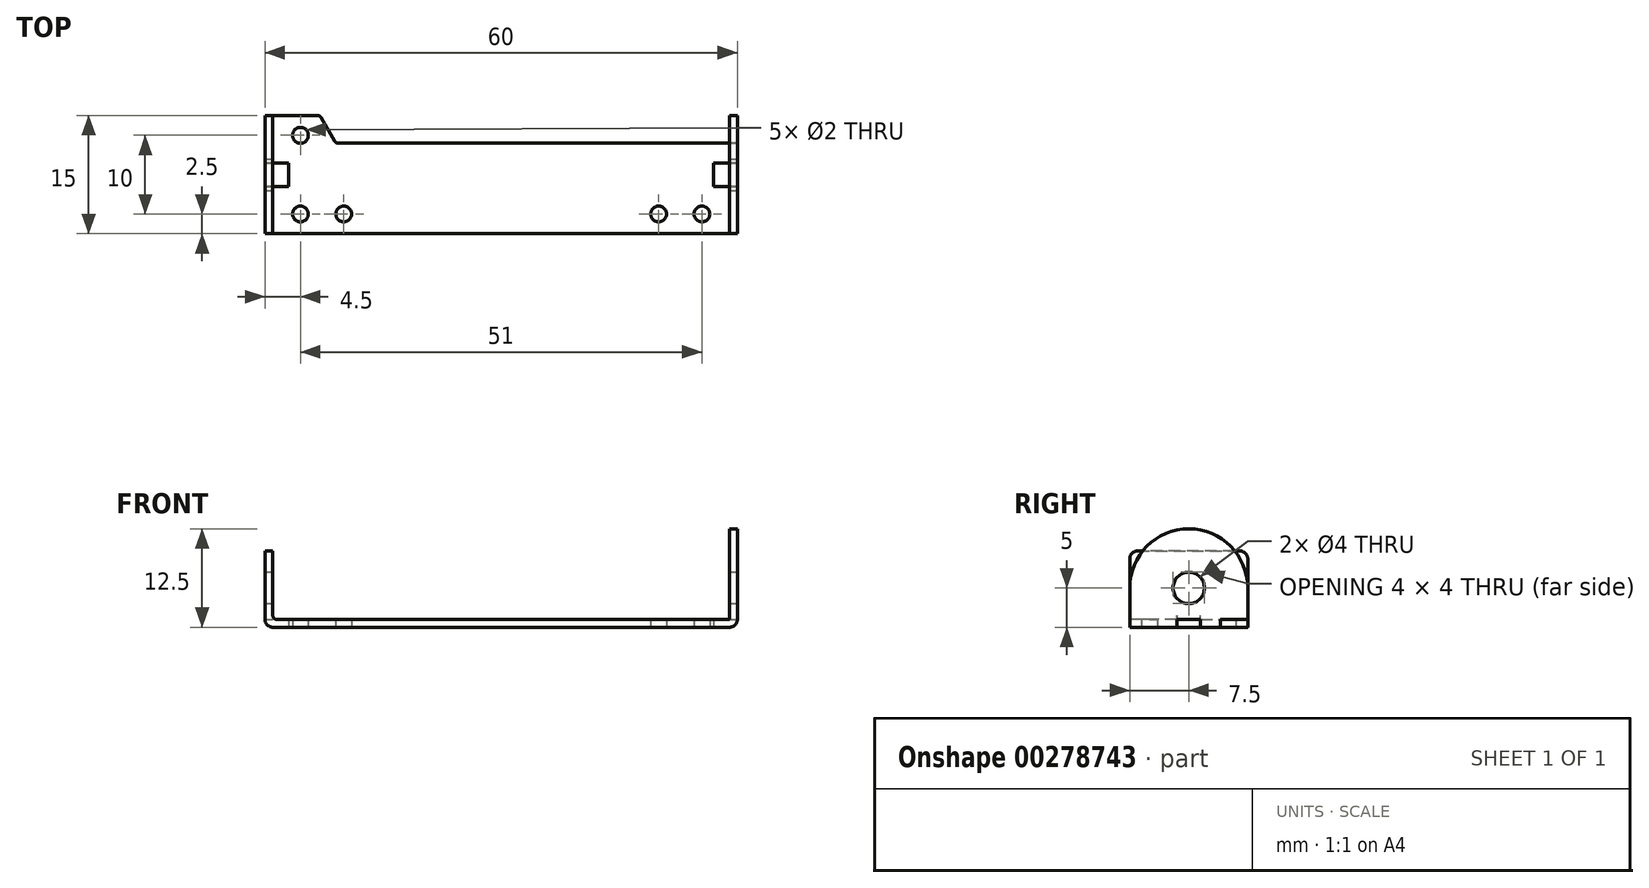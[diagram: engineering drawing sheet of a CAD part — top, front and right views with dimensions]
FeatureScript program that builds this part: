
annotation { "Feature Type Name" : "Feature", "Feature Type Description" : "" }
export const myFeature = defineFeature(function(context is Context, id is Id, definition is map)
    precondition{}
    {
        {
            var Q0;
            Q0=qCreatedBy(makeId("Top.planeOp"),FACE);
            var sketch = newSketch(context, id + "F0", { "sketchPlane" : qUnion([Q0])});
            skLineSegment(sketch, "E0.bottom", {"start": v(0, 0) * mm, "end": v(60, 0) * mm});
            skLineSegment(sketch, "E0.top", {"start": v(0, 15) * mm, "end": v(60, 15) * mm});
            skLineSegment(sketch, "E0.left", {"start": v(0, 0) * mm, "end": v(0, 15) * mm});
            skLineSegment(sketch, "E0.right", {"start": v(60, 0) * mm, "end": v(60, 15) * mm});
            skSolve(sketch);
        }
        {
            var Q0;
            Q0 = qSketchRegion(id + "F0", true);
            extrude(context, id + "F1", {"entities" : qUnion([Q0]), "depth" : 1 * mm});
        }
        {
            var Q0;
            Q0=makeQuery(id+"F1.opExtrude","CAP_FACE",FACE,{"disambiguationData":[OSD([sQuery(id+"F0.wireOp",EDGE,"E0.bottom"),sQuery(id+"F0.wireOp",EDGE,"E0.top"),sQuery(id+"F0.wireOp",EDGE,"E0.left"),sQuery(id+"F0.wireOp",EDGE,"E0.right")])],"isStart":false});
            var sketch = newSketch(context, id + "F2", { "sketchPlane" : qUnion([Q0])});
            skLineSegment(sketch, "E1.bottom", {"start": v(0, 15) * mm, "end": v(1, 15) * mm});
            skLineSegment(sketch, "E1.top", {"start": v(0, 0) * mm, "end": v(1, 0) * mm});
            skLineSegment(sketch, "E1.left", {"start": v(0, 15) * mm, "end": v(0, 0) * mm});
            skLineSegment(sketch, "E1.right", {"start": v(1, 15) * mm, "end": v(1, 0) * mm});
            skSolve(sketch);
        }
        {
            var Q0;
            Q0=makeQuery(id+"F2.imprint","IMPRINT",FACE,{"disambiguationData":[TD([[makeQuery(id+"F2.imprint","IMPRINT",EDGE,{"derivedFrom":sQuery(id+"F2.wireOp",EDGE,"E1.bottom")}),-1.0]])]});
            extrude(context, id + "F3", {"entities" : qUnion([Q0]), "operationType" : NewBodyOperationType.ADD, "depth" : 8.7 * mm});
        }
        {
            var Q0;
            Q0=makeQuery(id+"F1.opExtrude","CAP_FACE",FACE,{"disambiguationData":[OSD([sQuery(id+"F0.wireOp",EDGE,"E0.bottom"),sQuery(id+"F0.wireOp",EDGE,"E0.top"),sQuery(id+"F0.wireOp",EDGE,"E0.left"),sQuery(id+"F0.wireOp",EDGE,"E0.right")])],"isStart":false});
            var sketch = newSketch(context, id + "F4", { "sketchPlane" : qUnion([Q0])});
            skLineSegment(sketch, "E2.bottom", {"start": v(60, 0) * mm, "end": v(59, 0) * mm});
            skLineSegment(sketch, "E2.top", {"start": v(60, 15) * mm, "end": v(59, 15) * mm});
            skLineSegment(sketch, "E2.left", {"start": v(60, 0) * mm, "end": v(60, 15) * mm});
            skLineSegment(sketch, "E2.right", {"start": v(59, 0) * mm, "end": v(59, 15) * mm});
            skSolve(sketch);
        }
        {
            var Q0;
            Q0 = qSketchRegion(id + "F4", true);
            extrude(context, id + "F5", {"entities" : qUnion([Q0]), "operationType" : NewBodyOperationType.ADD, "depth" : 11.5 * mm});
        }
        {
            var Q0;
            Q0=makeQuery(id+"F1.opExtrude","CAP_FACE",FACE,{"disambiguationData":[OSD([sQuery(id+"F0.wireOp",EDGE,"E0.bottom"),sQuery(id+"F0.wireOp",EDGE,"E0.top"),sQuery(id+"F0.wireOp",EDGE,"E0.left"),sQuery(id+"F0.wireOp",EDGE,"E0.right")])],"isStart":true});
            var sketch = newSketch(context, id + "F6", { "sketchPlane" : qUnion([Q0])});
            skLineSegment(sketch, "E3", {"start": v(0, -7.5) * mm, "end": v(60, -7.5) * mm, "construction": true});
            skLineSegment(sketch, "E4", {"start": v(30, 0) * mm, "end": v(30, -15) * mm, "construction": true});
            skLineSegment(sketch, "E5.bottom", {"start": v(0, -6) * mm, "end": v(3, -6) * mm});
            skLineSegment(sketch, "E5.top", {"start": v(0, -9) * mm, "end": v(3, -9) * mm});
            skLineSegment(sketch, "E5.left", {"start": v(0, -6) * mm, "end": v(0, -9) * mm});
            skLineSegment(sketch, "E5.right", {"start": v(3, -6) * mm, "end": v(3, -9) * mm});
            skCircle(sketch, "E6", {"center": v(4.5, -2.5) * mm, "radius": 1 * mm});
            skCircle(sketch, "E7", {"center": v(10, -2.5) * mm, "radius": 1 * mm});
            skCircle(sketch, "E8.MirrorC", {"center": v(50, -2.5) * mm, "radius": 1 * mm});
            skCircle(sketch, "E9.MirrorC", {"center": v(55.5, -2.5) * mm, "radius": 1 * mm});
            skLineSegment(sketch, "E10.MirrorCS", {"start": v(57, -6) * mm, "end": v(57, -9) * mm});
            skLineSegment(sketch, "E11.MirrorCS", {"start": v(60, -6) * mm, "end": v(57, -6) * mm});
            skLineSegment(sketch, "E12.MirrorCS", {"start": v(60, -6) * mm, "end": v(60, -9) * mm});
            skLineSegment(sketch, "E13.MirrorCS", {"start": v(60, -9) * mm, "end": v(57, -9) * mm});
            skCircle(sketch, "E14.MirrorC", {"center": v(4.5, -12.5) * mm, "radius": 1 * mm});
            skLineSegment(sketch, "E15", {"start": v(7, -15) * mm, "end": v(9, -11.5) * mm});
            skLineSegment(sketch, "E16", {"start": v(9, -11.5) * mm, "end": v(60, -11.5) * mm});
            skLineSegment(sketch, "E17", {"start": v(7, -15) * mm, "end": v(60, -15) * mm});
            skLineSegment(sketch, "E18", {"start": v(60, -15) * mm, "end": v(60, -11.5) * mm});
            skSolve(sketch);
        }
        {
            var Q0;
            Q0 = qSketchRegion(id + "F6", true);
            var Q1;
            Q1=makeQuery(id+"F1.opExtrude","CAP_FACE",FACE,{"disambiguationData":[OSD([sQuery(id+"F0.wireOp",EDGE,"E0.bottom"),sQuery(id+"F0.wireOp",EDGE,"E0.top"),sQuery(id+"F0.wireOp",EDGE,"E0.left"),sQuery(id+"F0.wireOp",EDGE,"E0.right")])],"isStart":false});
            extrude(context, id + "F7", {"entities" : qUnion([Q0]), "operationType" : NewBodyOperationType.REMOVE, "endBound" : BoundingType.UP_TO_SURFACE, "oppositeDirection" : true, "endBoundEntityFace" : qUnion([Q1]), "depth" : 25 * mm});
        }
        {
            var Q0;
            Q0=makeQuery(id+"F5.opExtrude","CAP_EDGE",EDGE,{"disambiguationData":[OSD([sQuery(id+"F4.wireOp",EDGE,"E2.bottom")])],"isStart":false});
            var Q1;
            Q1=makeQuery(id+"F5.opExtrude","CAP_EDGE",EDGE,{"disambiguationData":[OSD([sQuery(id+"F4.wireOp",EDGE,"E2.top")])],"isStart":false});
            fillet(context, id + "F8", {"entities" : qUnion([Q0, Q1]), "radius" : 7.5 * mm, "tangentPropagation" : true, "allowEdgeOverflow" : false});
        }
        {
            var Q0;
            {var subQ0=sQuery(id+"F6.wireOp",EDGE,"E11.MirrorCS");var subQ1=sQuery(id+"F0.wireOp",EDGE,"E0.right");var subQ2=sQuery(id+"F0.wireOp",EDGE,"E0.left");var subQ3=sQuery(id+"F0.wireOp",EDGE,"E0.top");var subQ4=sQuery(id+"F0.wireOp",EDGE,"E0.bottom");var subQ5=sQuery(id+"F4.wireOp",EDGE,"E2.right");Q0=makeQuery(id+"F7.boolean.opBoolean","SPLIT",EDGE,{"disambiguationData":[TD([makeQuery(id+"F1.opExtrude","SWEPT_FACE",FACE,{"disambiguationData":[OSD([subQ4])]}),makeQuery(id+"F1.opExtrude","CAP_FACE",FACE,{"disambiguationData":[OSD([subQ4,subQ3,subQ2,subQ1])],"isStart":false}),makeQuery(id+"F3.opExtrude","SWEPT_FACE",FACE,{"disambiguationData":[OSD([sQuery(id+"F2.wireOp",EDGE,"E1.top")])]}),makeQuery(id+"F5.opExtrude","SWEPT_FACE",FACE,{"disambiguationData":[OSD([sQuery(id+"F4.wireOp",EDGE,"E2.bottom")])]}),makeQuery(id+"F5.opExtrude","SWEPT_FACE",FACE,{"disambiguationData":[OSD([subQ5])]}),makeQuery(id+"F7.opExtrude","SWEPT_FACE",FACE,{"disambiguationData":[OSD([subQ0])]}),makeQuery(id+"F7.opExtrude","CAP_FACE",FACE,{"disambiguationData":[OSD([subQ4,subQ3,subQ2,subQ1]),ownerDisambiguation([makeQuery(id+"F7.opExtrude","SWEPT_BODY",BODY,{"disambiguationData":[OSD([sQuery(id+"F6.wireOp",EDGE,"E10.MirrorCS"),subQ0,sQuery(id+"F6.wireOp",EDGE,"E12.MirrorCS"),sQuery(id+"F6.wireOp",EDGE,"E13.MirrorCS")])]})])],"isStart":false})])],"derivedFrom":makeQuery(id+"F5.opExtrude","CAP_EDGE",EDGE,{"disambiguationData":[OSD([subQ5])],"isStart":true})});}
            var Q1;
            {var subQ0=sQuery(id+"F6.wireOp",EDGE,"E16");var subQ1=sQuery(id+"F6.wireOp",EDGE,"E13.MirrorCS");var subQ2=sQuery(id+"F4.wireOp",EDGE,"E2.right");var subQ3=sQuery(id+"F0.wireOp",EDGE,"E0.right");var subQ4=sQuery(id+"F0.wireOp",EDGE,"E0.left");var subQ5=sQuery(id+"F0.wireOp",EDGE,"E0.top");var subQ6=sQuery(id+"F0.wireOp",EDGE,"E0.bottom");Q1=makeQuery(id+"F7.boolean.opBoolean","SPLIT",EDGE,{"disambiguationData":[TD([makeQuery(id+"F1.opExtrude","CAP_FACE",FACE,{"disambiguationData":[OSD([subQ6,subQ5,subQ4,subQ3])],"isStart":false}),makeQuery(id+"F5.opExtrude","SWEPT_FACE",FACE,{"disambiguationData":[OSD([subQ2])]}),makeQuery(id+"F7.opExtrude","SWEPT_FACE",FACE,{"disambiguationData":[OSD([subQ1])]}),makeQuery(id+"F7.opExtrude","SWEPT_FACE",FACE,{"disambiguationData":[OSD([subQ0])]}),makeQuery(id+"F7.opExtrude","CAP_FACE",FACE,{"disambiguationData":[OSD([subQ6,subQ5,subQ4,subQ3]),ownerDisambiguation([makeQuery(id+"F7.opExtrude","SWEPT_BODY",BODY,{"disambiguationData":[OSD([sQuery(id+"F6.wireOp",EDGE,"E10.MirrorCS"),sQuery(id+"F6.wireOp",EDGE,"E11.MirrorCS"),sQuery(id+"F6.wireOp",EDGE,"E12.MirrorCS"),subQ1])]})])],"isStart":false}),makeQuery(id+"F7.opExtrude","CAP_FACE",FACE,{"disambiguationData":[OSD([subQ6,subQ5,subQ4,subQ3]),ownerDisambiguation([makeQuery(id+"F7.opExtrude","SWEPT_BODY",BODY,{"disambiguationData":[OSD([sQuery(id+"F6.wireOp",EDGE,"E15"),subQ0,sQuery(id+"F6.wireOp",EDGE,"E17"),sQuery(id+"F6.wireOp",EDGE,"E18")])]})])],"isStart":false})])],"derivedFrom":makeQuery(id+"F5.opExtrude","CAP_EDGE",EDGE,{"disambiguationData":[OSD([subQ2])],"isStart":true})});}
            var Q2;
            {var subQ0=sQuery(id+"F2.wireOp",EDGE,"E1.right");var subQ1=sQuery(id+"F0.wireOp",EDGE,"E0.right");var subQ2=sQuery(id+"F0.wireOp",EDGE,"E0.left");var subQ3=sQuery(id+"F0.wireOp",EDGE,"E0.top");var subQ4=sQuery(id+"F0.wireOp",EDGE,"E0.bottom");var subQ5=sQuery(id+"F6.wireOp",EDGE,"E5.bottom");Q2=makeQuery(id+"F7.boolean.opBoolean","SPLIT",EDGE,{"disambiguationData":[TD([makeQuery(id+"F1.opExtrude","SWEPT_FACE",FACE,{"disambiguationData":[OSD([subQ4])]}),makeQuery(id+"F1.opExtrude","CAP_FACE",FACE,{"disambiguationData":[OSD([subQ4,subQ3,subQ2,subQ1])],"isStart":false}),makeQuery(id+"F3.opExtrude","SWEPT_FACE",FACE,{"disambiguationData":[OSD([sQuery(id+"F2.wireOp",EDGE,"E1.top")])]}),makeQuery(id+"F3.opExtrude","SWEPT_FACE",FACE,{"disambiguationData":[OSD([subQ0])]}),makeQuery(id+"F5.opExtrude","SWEPT_FACE",FACE,{"disambiguationData":[OSD([sQuery(id+"F4.wireOp",EDGE,"E2.bottom")])]}),makeQuery(id+"F7.opExtrude","SWEPT_FACE",FACE,{"disambiguationData":[OSD([subQ5])]}),makeQuery(id+"F7.opExtrude","CAP_FACE",FACE,{"disambiguationData":[OSD([subQ4,subQ3,subQ2,subQ1]),ownerDisambiguation([makeQuery(id+"F7.opExtrude","SWEPT_BODY",BODY,{"disambiguationData":[OSD([subQ5,sQuery(id+"F6.wireOp",EDGE,"E5.top"),sQuery(id+"F6.wireOp",EDGE,"E5.left"),sQuery(id+"F6.wireOp",EDGE,"E5.right")])]})])],"isStart":false})])],"derivedFrom":makeQuery(id+"F3.opExtrude","CAP_EDGE",EDGE,{"disambiguationData":[OSD([subQ0])],"isStart":true})});}
            var Q3;
            {var subQ0=sQuery(id+"F2.wireOp",EDGE,"E1.right");var subQ1=sQuery(id+"F6.wireOp",EDGE,"E5.top");var subQ2=sQuery(id+"F0.wireOp",EDGE,"E0.top");var subQ3=sQuery(id+"F0.wireOp",EDGE,"E0.right");var subQ4=sQuery(id+"F0.wireOp",EDGE,"E0.left");var subQ5=sQuery(id+"F0.wireOp",EDGE,"E0.bottom");Q3=makeQuery(id+"F7.boolean.opBoolean","SPLIT",EDGE,{"disambiguationData":[TD([makeQuery(id+"F1.opExtrude","CAP_FACE",FACE,{"disambiguationData":[OSD([subQ5,subQ2,subQ4,subQ3])],"isStart":false}),makeQuery(id+"F1.opExtrude","SWEPT_FACE",FACE,{"disambiguationData":[OSD([subQ2])]}),makeQuery(id+"F3.opExtrude","SWEPT_FACE",FACE,{"disambiguationData":[OSD([sQuery(id+"F2.wireOp",EDGE,"E1.bottom")])]}),makeQuery(id+"F3.opExtrude","SWEPT_FACE",FACE,{"disambiguationData":[OSD([subQ0])]}),makeQuery(id+"F5.opExtrude","SWEPT_FACE",FACE,{"disambiguationData":[OSD([sQuery(id+"F4.wireOp",EDGE,"E2.top")])]}),makeQuery(id+"F7.opExtrude","SWEPT_FACE",FACE,{"disambiguationData":[OSD([subQ1])]}),makeQuery(id+"F7.opExtrude","CAP_FACE",FACE,{"disambiguationData":[OSD([subQ5,subQ2,subQ4,subQ3]),ownerDisambiguation([makeQuery(id+"F7.opExtrude","SWEPT_BODY",BODY,{"disambiguationData":[OSD([sQuery(id+"F6.wireOp",EDGE,"E5.bottom"),subQ1,sQuery(id+"F6.wireOp",EDGE,"E5.left"),sQuery(id+"F6.wireOp",EDGE,"E5.right")])]})])],"isStart":false})])],"derivedFrom":makeQuery(id+"F3.opExtrude","CAP_EDGE",EDGE,{"disambiguationData":[OSD([subQ0])],"isStart":true})});}
            var Q4;
            Q4=makeQuery(id+"F7.boolean.opBoolean","COPY",EDGE,{"derivedFrom":makeQuery(id+"F7.opExtrude","SWEPT_EDGE",EDGE,{"disambiguationData":[OSD([sQuery(id+"F0.wireOp",EDGE,"E0.top"),sQuery(id+"F6.wireOp",EDGE,"E15"),sQuery(id+"F6.wireOp",EDGE,"E17")])]})});
            var Q5;
            Q5=makeQuery(id+"F7.boolean.opBoolean","COPY",EDGE,{"derivedFrom":makeQuery(id+"F7.opExtrude","SWEPT_EDGE",EDGE,{"disambiguationData":[OSD([sQuery(id+"F6.wireOp",EDGE,"E15"),sQuery(id+"F6.wireOp",EDGE,"E16")])]})});
            fillet(context, id + "F9", {"entities" : qUnion([Q0, Q1, Q2, Q3, Q4, Q5]), "radius" : 0.5 * mm, "tangentPropagation" : true, "allowEdgeOverflow" : false});
        }
        {
            var Q0;
            Q0=makeQuery(id+"F1.opExtrude","CAP_EDGE",EDGE,{"disambiguationData":[OSD([sQuery(id+"F0.wireOp",EDGE,"E0.right")])],"isStart":true});
            var Q1;
            Q1=makeQuery(id+"F1.opExtrude","CAP_EDGE",EDGE,{"disambiguationData":[OSD([sQuery(id+"F0.wireOp",EDGE,"E0.left")])],"isStart":true});
            var Q2;
            Q2=makeQuery(id+"F3.opExtrude","CAP_EDGE",EDGE,{"disambiguationData":[OSD([sQuery(id+"F2.wireOp",EDGE,"E1.top")])],"isStart":false});
            var Q3;
            Q3=makeQuery(id+"F3.opExtrude","CAP_EDGE",EDGE,{"disambiguationData":[OSD([sQuery(id+"F2.wireOp",EDGE,"E1.bottom")])],"isStart":false});
            fillet(context, id + "F10", {"entities" : qUnion([Q0, Q1, Q2, Q3]), "radius" : 1 * mm, "tangentPropagation" : true, "allowEdgeOverflow" : false});
        }
        {
            var Q0;
            Q0=makeQuery(id+"F5.boolean.opBoolean","MERGE",FACE,{"derivedFrom":[makeQuery(id+"F1.opExtrude","SWEPT_FACE",FACE,{"disambiguationData":[OSD([sQuery(id+"F0.wireOp",EDGE,"E0.right")])]}),makeQuery(id+"F5.opExtrude","SWEPT_FACE",FACE,{"disambiguationData":[OSD([sQuery(id+"F4.wireOp",EDGE,"E2.left")])]})]});
            var sketch = newSketch(context, id + "F11", { "sketchPlane" : qUnion([Q0])});
            skCircle(sketch, "E19", {"center": v(7.5, 5) * mm, "radius": 2 * mm});
            skSolve(sketch);
        }
        {
            var Q0;
            Q0 = qSketchRegion(id + "F11", true);
            extrude(context, id + "F12", {"entities" : qUnion([Q0]), "operationType" : NewBodyOperationType.REMOVE, "endBound" : BoundingType.THROUGH_ALL, "oppositeDirection" : true, "depth" : 25 * mm});
        }
    });
